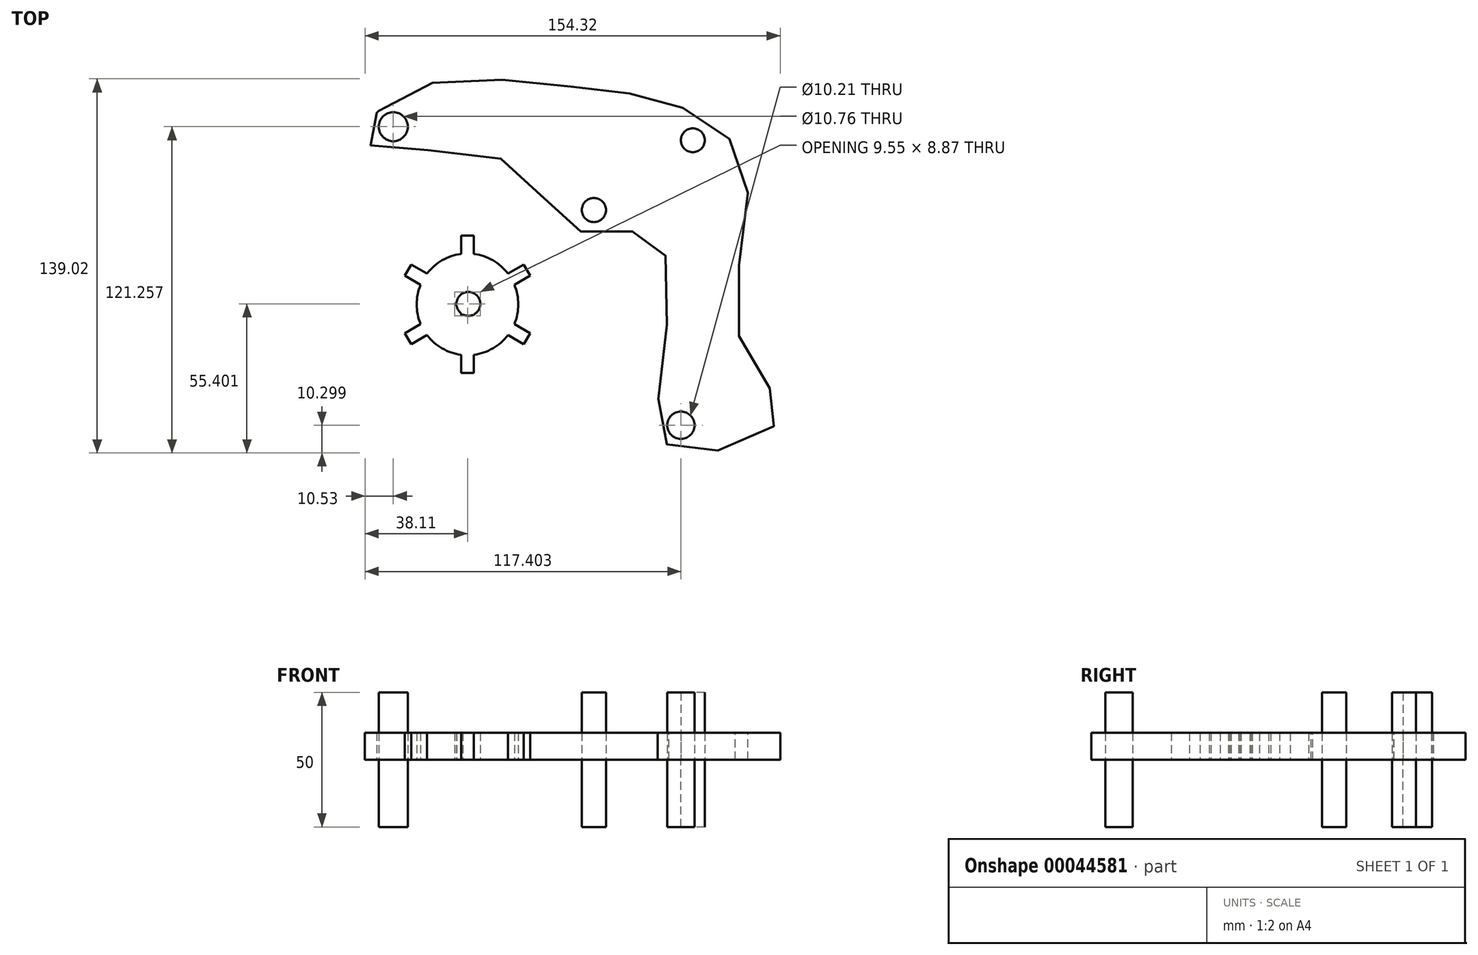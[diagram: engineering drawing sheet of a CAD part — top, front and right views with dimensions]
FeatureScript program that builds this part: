
annotation { "Feature Type Name" : "Feature", "Feature Type Description" : "" }
export const myFeature = defineFeature(function(context is Context, id is Id, definition is map)
    precondition{}
    {
        {
            var Q0;
            Q0=qCreatedBy(makeId("Top.planeOp"),FACE);
            var sketch = newSketch(context, id + "F0", { "sketchPlane" : qUnion([Q0])});
            skFitSpline(sketch, "E0", {"points": [v(-58.25, 62.71) * mm, v(0, 65.43) * mm, v(41.48, 58.63) * mm, v(69.05, 33.78) * mm, v(66.67, -28.5) * mm, v(81.3, -58.46) * mm, v(43.86, -70.37) * mm, v(37.05, -45.86) * mm, v(35.35, 8.93) * mm, v(6.08, 11.66) * mm, v(-21.15, 37.86) * mm, v(-71.52, 44) * mm, v(-58.25, 62.71) * mm]});
            skCircle(sketch, "E1", {"center": v(49.31, 45.07) * mm, "radius": 8 * mm});
            skCircle(sketch, "E2", {"center": v(44.88, -60.84) * mm, "radius": 8 * mm});
            skCircle(sketch, "E3", {"center": v(-62, 50.12) * mm, "radius": 8 * mm});
            skCircle(sketch, "E4", {"center": v(12.55, 19.14) * mm, "radius": 8 * mm});
            skLineSegment(sketch, "E5.rect.bottom", {"start": v(-32.04, -41.44) * mm, "end": v(-36.8, -41.44) * mm});
            skLineSegment(sketch, "E5.rect.top", {"start": v(-32.04, 9.61) * mm, "end": v(-36.8, 9.61) * mm});
            skLineSegment(sketch, "E5.rect.left", {"start": v(-32.04, -41.44) * mm, "end": v(-32.04, 9.61) * mm});
            skLineSegment(sketch, "E5.rect.right", {"start": v(-36.8, -41.44) * mm, "end": v(-36.8, 9.61) * mm});
            skPoint(sketch, "E5.rect.middle", {"position": v(-34.42, -15.91) * mm});
            skLineSegment(sketch, "E6.1.0", {"start": v(-55.34, -1.09) * mm, "end": v(-11.12, -26.61) * mm});
            skLineSegment(sketch, "E6.1.1", {"start": v(-57.72, -5.21) * mm, "end": v(-13.5, -30.74) * mm});
            skLineSegment(sketch, "E6.1.3", {"start": v(-13.5, -30.74) * mm, "end": v(-11.12, -26.61) * mm});
            skLineSegment(sketch, "E6.1.4", {"start": v(-57.72, -5.21) * mm, "end": v(-55.34, -1.09) * mm});
            skLineSegment(sketch, "E6.2.0", {"start": v(-11.12, -5.21) * mm, "end": v(-55.34, -30.74) * mm});
            skLineSegment(sketch, "E6.2.1", {"start": v(-13.5, -1.09) * mm, "end": v(-57.72, -26.61) * mm});
            skLineSegment(sketch, "E6.2.3", {"start": v(-57.72, -26.61) * mm, "end": v(-55.34, -30.74) * mm});
            skLineSegment(sketch, "E6.2.4", {"start": v(-13.5, -1.09) * mm, "end": v(-11.12, -5.21) * mm});
            skLineSegment(sketch, "E6.anchor1", {"start": v(-34.42, -15.91) * mm, "end": v(-36.8, -41.44) * mm, "construction": true});
            skLineSegment(sketch, "E6.anchor2", {"start": v(-34.42, -15.91) * mm, "end": v(-11.12, -5.21) * mm, "construction": true});
            skCircle(sketch, "E7", {"center": v(-34.42, -15.91) * mm, "radius": 18.88 * mm});
            skFitSpline(sketch, "E8.0", {"points": [v(-58.74, 59.44) * mm, v(-57.05, 60.37) * mm, v(-55.3, 61.2) * mm, v(-52.87, 62.2) * mm, v(-49.66, 63.22) * mm, v(-45.57, 64.13) * mm, v(-39.84, 64.96) * mm, v(-32.27, 65.36) * mm, v(-22.81, 65.05) * mm, v(-14.88, 64.37) * mm, v(-8.64, 63.71) * mm, v(-4.05, 63.2) * mm, v(0.42, 62.72) * mm, v(4.72, 62.28) * mm, v(8.85, 61.87) * mm, v(14.16, 61.33) * mm, v(20.48, 60.62) * mm, v(26.47, 59.7) * mm, v(31.13, 58.77) * mm, v(34.6, 57.95) * mm, v(38.03, 56.99) * mm, v(41.46, 55.86) * mm, v(44.9, 54.54) * mm, v(49.38, 52.54) * mm, v(54.68, 49.54) * mm, v(59.21, 45.83) * mm, v(62.18, 42.41) * mm, v(64.05, 39.62) * mm, v(65.27, 37.1) * mm, v(66.03, 34.92) * mm, v(66.48, 33.23) * mm, v(66.82, 31.44) * mm, v(67.12, 28.92) * mm, v(67.24, 25.54) * mm, v(67.04, 21.17) * mm, v(66.4, 15) * mm, v(65.09, 6.83) * mm, v(63.68, -1.66) * mm, v(62.84, -8.44) * mm, v(62.45, -13.5) * mm, v(62.39, -18.46) * mm, v(62.69, -22.5) * mm, v(63.2, -25.67) * mm, v(63.73, -28) * mm, v(64.43, -30.27) * mm, v(65.27, -32.44) * mm, v(66.24, -34.52) * mm, v(67.66, -37.18) * mm, v(69.6, -40.29) * mm, v(72.04, -43.7) * mm, v(74.37, -46.83) * mm, v(76.42, -49.69) * mm, v(78.02, -52.25) * mm, v(78.81, -54.07) * mm, v(79.1, -55.28) * mm, v(79.17, -56.06) * mm, v(79.11, -56.63) * mm, v(79, -57.07) * mm, v(78.87, -57.41) * mm, v(78.7, -57.77) * mm, v(78.4, -58.29) * mm, v(77.85, -59) * mm, v(76.95, -59.9) * mm, v(75.44, -61.12) * mm, v(73.03, -62.66) * mm, v(69.5, -64.35) * mm, v(65.55, -65.84) * mm, v(61.35, -67.04) * mm, v(57.1, -67.93) * mm, v(52.97, -68.44) * mm, v(49.8, -68.53) * mm, v(47.55, -68.4) * mm, v(46.02, -68.19) * mm, v(44.7, -67.88) * mm, v(43.6, -67.49) * mm, v(42.69, -67.02) * mm, v(41.93, -66.5) * mm, v(41.3, -65.89) * mm, v(40.56, -64.95) * mm, v(39.82, -63.49) * mm, v(39.22, -61.13) * mm, v(38.94, -58.18) * mm, v(38.95, -54.7) * mm, v(39.2, -50.76) * mm, v(39.65, -46.37) * mm, v(40.22, -41.6) * mm, v(41.05, -34.85) * mm, v(41.91, -27.74) * mm, v(42.58, -20.62) * mm, v(42.94, -15.37) * mm, v(43.1, -10.3) * mm, v(43, -5.48) * mm, v(42.58, -1) * mm, v(41.77, 3.1) * mm, v(40.67, 6.13) * mm, v(39.46, 8.3) * mm, v(38.54, 9.53) * mm, v(37.7, 10.41) * mm, v(37, 11.02) * mm, v(36.27, 11.57) * mm, v(35.24, 12.2) * mm, v(33.9, 12.81) * mm, v(31.66, 13.5) * mm, v(28.76, 13.87) * mm, v(25.2, 13.87) * mm, v(21.6, 13.63) * mm, v(18.01, 13.33) * mm, v(14.55, 13.12) * mm, v(11.87, 13.16) * mm, v(9.9, 13.37) * mm, v(8.54, 13.63) * mm, v(7.5, 13.94) * mm, v(6.73, 14.25) * mm, v(5.98, 14.6) * mm, v(5.06, 15.13) * mm, v(3.63, 16.17) * mm, v(1.87, 17.82) * mm, v(-0.22, 20.29) * mm, v(-2.33, 23.13) * mm, v(-4.53, 26.2) * mm, v(-6.91, 29.38) * mm, v(-9.56, 32.55) * mm, v(-12.08, 35.05) * mm, v(-14.34, 36.9) * mm, v(-16.16, 38.2) * mm, v(-17.8, 39.17) * mm, v(-19.18, 39.88) * mm, v(-20.62, 40.54) * mm, v(-22.5, 41.27) * mm, v(-24.84, 41.97) * mm, v(-27.27, 42.55) * mm, v(-30.6, 43.15) * mm, v(-34.88, 43.65) * mm, v(-40.14, 43.94) * mm, v(-45.39, 44.02) * mm, v(-50.5, 43.99) * mm, v(-55.34, 43.94) * mm, v(-59.77, 43.97) * mm, v(-63, 44.12) * mm, v(-65.21, 44.36) * mm, v(-66.66, 44.6) * mm, v(-67.86, 44.9) * mm, v(-68.62, 45.18) * mm, v(-69.07, 45.41) * mm, v(-69.32, 45.57) * mm, v(-69.5, 45.72) * mm, v(-69.61, 45.83) * mm, v(-69.7, 45.93) * mm, v(-69.77, 46.07) * mm, v(-69.85, 46.3) * mm, v(-69.9, 46.75) * mm, v(-69.82, 47.41) * mm, v(-69.59, 48.25) * mm, v(-69.04, 49.55) * mm, v(-67.92, 51.42) * mm, v(-65.92, 53.83) * mm, v(-63.38, 56.22) * mm, v(-60.9, 58.09) * mm, v(-58.74, 59.44) * mm, v(-57.05, 60.37) * mm, v(-55.3, 61.2) * mm]});
            skFitSpline(sketch, "E9.trimOffspring", {"points": [v(-58.74, 59.44) * mm, v(-57.05, 60.37) * mm, v(-55.3, 61.2) * mm, v(-52.87, 62.2) * mm, v(-49.66, 63.22) * mm, v(-45.57, 64.13) * mm, v(-39.84, 64.96) * mm, v(-32.27, 65.36) * mm, v(-22.81, 65.05) * mm, v(-14.88, 64.37) * mm, v(-8.64, 63.71) * mm, v(-4.05, 63.2) * mm, v(0.42, 62.72) * mm, v(4.72, 62.28) * mm, v(8.85, 61.87) * mm, v(14.16, 61.33) * mm, v(20.48, 60.62) * mm, v(26.47, 59.7) * mm, v(31.13, 58.77) * mm, v(34.6, 57.95) * mm, v(38.03, 56.99) * mm, v(41.46, 55.86) * mm, v(44.9, 54.54) * mm, v(49.38, 52.54) * mm, v(54.68, 49.54) * mm, v(59.21, 45.83) * mm, v(62.18, 42.41) * mm, v(64.05, 39.62) * mm, v(65.27, 37.1) * mm, v(66.03, 34.92) * mm, v(66.48, 33.23) * mm, v(66.82, 31.44) * mm, v(67.12, 28.92) * mm, v(67.24, 25.54) * mm, v(67.04, 21.17) * mm, v(66.4, 15) * mm, v(65.09, 6.83) * mm, v(63.68, -1.66) * mm, v(62.84, -8.44) * mm, v(62.45, -13.5) * mm, v(62.39, -18.46) * mm, v(62.69, -22.5) * mm, v(63.2, -25.67) * mm, v(63.73, -28) * mm, v(64.43, -30.27) * mm, v(65.27, -32.44) * mm, v(66.24, -34.52) * mm, v(67.66, -37.18) * mm, v(69.6, -40.29) * mm, v(72.04, -43.7) * mm, v(74.37, -46.83) * mm, v(76.42, -49.69) * mm, v(78.02, -52.25) * mm, v(78.81, -54.07) * mm, v(79.1, -55.28) * mm, v(79.17, -56.06) * mm, v(79.11, -56.63) * mm, v(79, -57.07) * mm, v(78.87, -57.41) * mm, v(78.7, -57.77) * mm, v(78.4, -58.29) * mm, v(77.85, -59) * mm, v(76.95, -59.9) * mm, v(75.44, -61.12) * mm, v(73.03, -62.66) * mm, v(69.5, -64.35) * mm, v(65.55, -65.84) * mm, v(61.35, -67.04) * mm, v(57.1, -67.93) * mm, v(52.97, -68.44) * mm, v(49.8, -68.53) * mm, v(47.55, -68.4) * mm, v(46.02, -68.19) * mm, v(44.7, -67.88) * mm, v(43.6, -67.49) * mm, v(42.69, -67.02) * mm, v(41.93, -66.5) * mm, v(41.3, -65.89) * mm, v(40.56, -64.95) * mm, v(39.82, -63.49) * mm, v(39.22, -61.13) * mm, v(38.94, -58.18) * mm, v(38.95, -54.7) * mm, v(39.2, -50.76) * mm, v(39.65, -46.37) * mm, v(40.22, -41.6) * mm, v(41.05, -34.85) * mm, v(41.91, -27.74) * mm, v(42.58, -20.62) * mm, v(42.94, -15.37) * mm, v(43.1, -10.3) * mm, v(43, -5.48) * mm, v(42.58, -1) * mm, v(41.77, 3.1) * mm, v(40.67, 6.13) * mm, v(39.46, 8.3) * mm, v(38.54, 9.53) * mm, v(37.7, 10.41) * mm, v(37, 11.02) * mm, v(36.27, 11.57) * mm, v(35.24, 12.2) * mm, v(33.9, 12.81) * mm, v(31.66, 13.5) * mm, v(28.76, 13.87) * mm, v(25.2, 13.87) * mm, v(21.6, 13.63) * mm, v(18.01, 13.33) * mm, v(14.55, 13.12) * mm, v(11.87, 13.16) * mm, v(9.9, 13.37) * mm, v(8.54, 13.63) * mm, v(7.5, 13.94) * mm, v(6.73, 14.25) * mm, v(5.98, 14.6) * mm, v(5.06, 15.13) * mm, v(3.63, 16.17) * mm, v(1.87, 17.82) * mm, v(-0.22, 20.29) * mm, v(-2.33, 23.13) * mm, v(-4.53, 26.2) * mm, v(-6.91, 29.38) * mm, v(-9.56, 32.55) * mm, v(-12.08, 35.05) * mm, v(-14.34, 36.9) * mm, v(-16.16, 38.2) * mm, v(-17.8, 39.17) * mm, v(-19.18, 39.88) * mm, v(-20.62, 40.54) * mm, v(-22.5, 41.27) * mm, v(-24.84, 41.97) * mm, v(-27.27, 42.55) * mm, v(-30.6, 43.15) * mm, v(-34.88, 43.65) * mm, v(-40.14, 43.94) * mm, v(-45.39, 44.02) * mm, v(-50.5, 43.99) * mm, v(-55.34, 43.94) * mm, v(-59.77, 43.97) * mm, v(-63, 44.12) * mm, v(-65.21, 44.36) * mm, v(-66.66, 44.6) * mm, v(-67.86, 44.9) * mm, v(-68.62, 45.18) * mm, v(-69.07, 45.41) * mm, v(-69.32, 45.57) * mm, v(-69.5, 45.72) * mm, v(-69.61, 45.83) * mm, v(-69.7, 45.93) * mm, v(-69.77, 46.07) * mm, v(-69.85, 46.3) * mm, v(-69.9, 46.75) * mm, v(-69.82, 47.41) * mm, v(-69.59, 48.25) * mm, v(-69.04, 49.55) * mm, v(-67.92, 51.42) * mm, v(-65.92, 53.83) * mm, v(-63.38, 56.22) * mm, v(-60.9, 58.09) * mm, v(-58.74, 59.44) * mm, v(-57.05, 60.37) * mm, v(-55.3, 61.2) * mm]});
            skFitSpline(sketch, "E10.trimOffspring", {"points": [v(-58.74, 59.44) * mm, v(-57.05, 60.37) * mm, v(-55.3, 61.2) * mm, v(-52.87, 62.2) * mm, v(-49.66, 63.22) * mm, v(-45.57, 64.13) * mm, v(-39.84, 64.96) * mm, v(-32.27, 65.36) * mm, v(-22.81, 65.05) * mm, v(-14.88, 64.37) * mm, v(-8.64, 63.71) * mm, v(-4.05, 63.2) * mm, v(0.42, 62.72) * mm, v(4.72, 62.28) * mm, v(8.85, 61.87) * mm, v(14.16, 61.33) * mm, v(20.48, 60.62) * mm, v(26.47, 59.7) * mm, v(31.13, 58.77) * mm, v(34.6, 57.95) * mm, v(38.03, 56.99) * mm, v(41.46, 55.86) * mm, v(44.9, 54.54) * mm, v(49.38, 52.54) * mm, v(54.68, 49.54) * mm, v(59.21, 45.83) * mm, v(62.18, 42.41) * mm, v(64.05, 39.62) * mm, v(65.27, 37.1) * mm, v(66.03, 34.92) * mm, v(66.48, 33.23) * mm, v(66.82, 31.44) * mm, v(67.12, 28.92) * mm, v(67.24, 25.54) * mm, v(67.04, 21.17) * mm, v(66.4, 15) * mm, v(65.09, 6.83) * mm, v(63.68, -1.66) * mm, v(62.84, -8.44) * mm, v(62.45, -13.5) * mm, v(62.39, -18.46) * mm, v(62.69, -22.5) * mm, v(63.2, -25.67) * mm, v(63.73, -28) * mm, v(64.43, -30.27) * mm, v(65.27, -32.44) * mm, v(66.24, -34.52) * mm, v(67.66, -37.18) * mm, v(69.6, -40.29) * mm, v(72.04, -43.7) * mm, v(74.37, -46.83) * mm, v(76.42, -49.69) * mm, v(78.02, -52.25) * mm, v(78.81, -54.07) * mm, v(79.1, -55.28) * mm, v(79.17, -56.06) * mm, v(79.11, -56.63) * mm, v(79, -57.07) * mm, v(78.87, -57.41) * mm, v(78.7, -57.77) * mm, v(78.4, -58.29) * mm, v(77.85, -59) * mm, v(76.95, -59.9) * mm, v(75.44, -61.12) * mm, v(73.03, -62.66) * mm, v(69.5, -64.35) * mm, v(65.55, -65.84) * mm, v(61.35, -67.04) * mm, v(57.1, -67.93) * mm, v(52.97, -68.44) * mm, v(49.8, -68.53) * mm, v(47.55, -68.4) * mm, v(46.02, -68.19) * mm, v(44.7, -67.88) * mm, v(43.6, -67.49) * mm, v(42.69, -67.02) * mm, v(41.93, -66.5) * mm, v(41.3, -65.89) * mm, v(40.56, -64.95) * mm, v(39.82, -63.49) * mm, v(39.22, -61.13) * mm, v(38.94, -58.18) * mm, v(38.95, -54.7) * mm, v(39.2, -50.76) * mm, v(39.65, -46.37) * mm, v(40.22, -41.6) * mm, v(41.05, -34.85) * mm, v(41.91, -27.74) * mm, v(42.58, -20.62) * mm, v(42.94, -15.37) * mm, v(43.1, -10.3) * mm, v(43, -5.48) * mm, v(42.58, -1) * mm, v(41.77, 3.1) * mm, v(40.67, 6.13) * mm, v(39.46, 8.3) * mm, v(38.54, 9.53) * mm, v(37.7, 10.41) * mm, v(37, 11.02) * mm, v(36.27, 11.57) * mm, v(35.24, 12.2) * mm, v(33.9, 12.81) * mm, v(31.66, 13.5) * mm, v(28.76, 13.87) * mm, v(25.2, 13.87) * mm, v(21.6, 13.63) * mm, v(18.01, 13.33) * mm, v(14.55, 13.12) * mm, v(11.87, 13.16) * mm, v(9.9, 13.37) * mm, v(8.54, 13.63) * mm, v(7.5, 13.94) * mm, v(6.73, 14.25) * mm, v(5.98, 14.6) * mm, v(5.06, 15.13) * mm, v(3.63, 16.17) * mm, v(1.87, 17.82) * mm, v(-0.22, 20.29) * mm, v(-2.33, 23.13) * mm, v(-4.53, 26.2) * mm, v(-6.91, 29.38) * mm, v(-9.56, 32.55) * mm, v(-12.08, 35.05) * mm, v(-14.34, 36.9) * mm, v(-16.16, 38.2) * mm, v(-17.8, 39.17) * mm, v(-19.18, 39.88) * mm, v(-20.62, 40.54) * mm, v(-22.5, 41.27) * mm, v(-24.84, 41.97) * mm, v(-27.27, 42.55) * mm, v(-30.6, 43.15) * mm, v(-34.88, 43.65) * mm, v(-40.14, 43.94) * mm, v(-45.39, 44.02) * mm, v(-50.5, 43.99) * mm, v(-55.34, 43.94) * mm, v(-59.77, 43.97) * mm, v(-63, 44.12) * mm, v(-65.21, 44.36) * mm, v(-66.66, 44.6) * mm, v(-67.86, 44.9) * mm, v(-68.62, 45.18) * mm, v(-69.07, 45.41) * mm, v(-69.32, 45.57) * mm, v(-69.5, 45.72) * mm, v(-69.61, 45.83) * mm, v(-69.7, 45.93) * mm, v(-69.77, 46.07) * mm, v(-69.85, 46.3) * mm, v(-69.9, 46.75) * mm, v(-69.82, 47.41) * mm, v(-69.59, 48.25) * mm, v(-69.04, 49.55) * mm, v(-67.92, 51.42) * mm, v(-65.92, 53.83) * mm, v(-63.38, 56.22) * mm, v(-60.9, 58.09) * mm, v(-58.74, 59.44) * mm, v(-57.05, 60.37) * mm, v(-55.3, 61.2) * mm]});
            skFitSpline(sketch, "E11.trimOffspring", {"points": [v(-58.74, 59.44) * mm, v(-57.05, 60.37) * mm, v(-55.3, 61.2) * mm, v(-52.87, 62.2) * mm, v(-49.66, 63.22) * mm, v(-45.57, 64.13) * mm, v(-39.84, 64.96) * mm, v(-32.27, 65.36) * mm, v(-22.81, 65.05) * mm, v(-14.88, 64.37) * mm, v(-8.64, 63.71) * mm, v(-4.05, 63.2) * mm, v(0.42, 62.72) * mm, v(4.72, 62.28) * mm, v(8.85, 61.87) * mm, v(14.16, 61.33) * mm, v(20.48, 60.62) * mm, v(26.47, 59.7) * mm, v(31.13, 58.77) * mm, v(34.6, 57.95) * mm, v(38.03, 56.99) * mm, v(41.46, 55.86) * mm, v(44.9, 54.54) * mm, v(49.38, 52.54) * mm, v(54.68, 49.54) * mm, v(59.21, 45.83) * mm, v(62.18, 42.41) * mm, v(64.05, 39.62) * mm, v(65.27, 37.1) * mm, v(66.03, 34.92) * mm, v(66.48, 33.23) * mm, v(66.82, 31.44) * mm, v(67.12, 28.92) * mm, v(67.24, 25.54) * mm, v(67.04, 21.17) * mm, v(66.4, 15) * mm, v(65.09, 6.83) * mm, v(63.68, -1.66) * mm, v(62.84, -8.44) * mm, v(62.45, -13.5) * mm, v(62.39, -18.46) * mm, v(62.69, -22.5) * mm, v(63.2, -25.67) * mm, v(63.73, -28) * mm, v(64.43, -30.27) * mm, v(65.27, -32.44) * mm, v(66.24, -34.52) * mm, v(67.66, -37.18) * mm, v(69.6, -40.29) * mm, v(72.04, -43.7) * mm, v(74.37, -46.83) * mm, v(76.42, -49.69) * mm, v(78.02, -52.25) * mm, v(78.81, -54.07) * mm, v(79.1, -55.28) * mm, v(79.17, -56.06) * mm, v(79.11, -56.63) * mm, v(79, -57.07) * mm, v(78.87, -57.41) * mm, v(78.7, -57.77) * mm, v(78.4, -58.29) * mm, v(77.85, -59) * mm, v(76.95, -59.9) * mm, v(75.44, -61.12) * mm, v(73.03, -62.66) * mm, v(69.5, -64.35) * mm, v(65.55, -65.84) * mm, v(61.35, -67.04) * mm, v(57.1, -67.93) * mm, v(52.97, -68.44) * mm, v(49.8, -68.53) * mm, v(47.55, -68.4) * mm, v(46.02, -68.19) * mm, v(44.7, -67.88) * mm, v(43.6, -67.49) * mm, v(42.69, -67.02) * mm, v(41.93, -66.5) * mm, v(41.3, -65.89) * mm, v(40.56, -64.95) * mm, v(39.82, -63.49) * mm, v(39.22, -61.13) * mm, v(38.94, -58.18) * mm, v(38.95, -54.7) * mm, v(39.2, -50.76) * mm, v(39.65, -46.37) * mm, v(40.22, -41.6) * mm, v(41.05, -34.85) * mm, v(41.91, -27.74) * mm, v(42.58, -20.62) * mm, v(42.94, -15.37) * mm, v(43.1, -10.3) * mm, v(43, -5.48) * mm, v(42.58, -1) * mm, v(41.77, 3.1) * mm, v(40.67, 6.13) * mm, v(39.46, 8.3) * mm, v(38.54, 9.53) * mm, v(37.7, 10.41) * mm, v(37, 11.02) * mm, v(36.27, 11.57) * mm, v(35.24, 12.2) * mm, v(33.9, 12.81) * mm, v(31.66, 13.5) * mm, v(28.76, 13.87) * mm, v(25.2, 13.87) * mm, v(21.6, 13.63) * mm, v(18.01, 13.33) * mm, v(14.55, 13.12) * mm, v(11.87, 13.16) * mm, v(9.9, 13.37) * mm, v(8.54, 13.63) * mm, v(7.5, 13.94) * mm, v(6.73, 14.25) * mm, v(5.98, 14.6) * mm, v(5.06, 15.13) * mm, v(3.63, 16.17) * mm, v(1.87, 17.82) * mm, v(-0.22, 20.29) * mm, v(-2.33, 23.13) * mm, v(-4.53, 26.2) * mm, v(-6.91, 29.38) * mm, v(-9.56, 32.55) * mm, v(-12.08, 35.05) * mm, v(-14.34, 36.9) * mm, v(-16.16, 38.2) * mm, v(-17.8, 39.17) * mm, v(-19.18, 39.88) * mm, v(-20.62, 40.54) * mm, v(-22.5, 41.27) * mm, v(-24.84, 41.97) * mm, v(-27.27, 42.55) * mm, v(-30.6, 43.15) * mm, v(-34.88, 43.65) * mm, v(-40.14, 43.94) * mm, v(-45.39, 44.02) * mm, v(-50.5, 43.99) * mm, v(-55.34, 43.94) * mm, v(-59.77, 43.97) * mm, v(-63, 44.12) * mm, v(-65.21, 44.36) * mm, v(-66.66, 44.6) * mm, v(-67.86, 44.9) * mm, v(-68.62, 45.18) * mm, v(-69.07, 45.41) * mm, v(-69.32, 45.57) * mm, v(-69.5, 45.72) * mm, v(-69.61, 45.83) * mm, v(-69.7, 45.93) * mm, v(-69.77, 46.07) * mm, v(-69.85, 46.3) * mm, v(-69.9, 46.75) * mm, v(-69.82, 47.41) * mm, v(-69.59, 48.25) * mm, v(-69.04, 49.55) * mm, v(-67.92, 51.42) * mm, v(-65.92, 53.83) * mm, v(-63.38, 56.22) * mm, v(-60.9, 58.09) * mm, v(-58.74, 59.44) * mm, v(-57.05, 60.37) * mm, v(-55.3, 61.2) * mm]});
            skCircle(sketch, "E12", {"center": v(-62, 50.12) * mm, "radius": 5.38 * mm});
            skCircle(sketch, "E13", {"center": v(12.55, 19.14) * mm, "radius": 4.5 * mm});
            skCircle(sketch, "E14", {"center": v(49.31, 45.07) * mm, "radius": 4.44 * mm});
            skCircle(sketch, "E15", {"center": v(44.88, -60.84) * mm, "radius": 5.1 * mm});
            skFitSpline(sketch, "E16.trimOffspring", {"points": [v(-58.74, 59.44) * mm, v(-57.05, 60.37) * mm, v(-55.3, 61.2) * mm, v(-52.87, 62.2) * mm, v(-49.66, 63.22) * mm, v(-45.57, 64.13) * mm, v(-39.84, 64.96) * mm, v(-32.27, 65.36) * mm, v(-22.81, 65.05) * mm, v(-14.88, 64.37) * mm, v(-8.64, 63.71) * mm, v(-4.05, 63.2) * mm, v(0.42, 62.72) * mm, v(4.72, 62.28) * mm, v(8.85, 61.87) * mm, v(14.16, 61.33) * mm, v(20.48, 60.62) * mm, v(26.47, 59.7) * mm, v(31.13, 58.77) * mm, v(34.6, 57.95) * mm, v(38.03, 56.99) * mm, v(41.46, 55.86) * mm, v(44.9, 54.54) * mm, v(49.38, 52.54) * mm, v(54.68, 49.54) * mm, v(59.21, 45.83) * mm, v(62.18, 42.41) * mm, v(64.05, 39.62) * mm, v(65.27, 37.1) * mm, v(66.03, 34.92) * mm, v(66.48, 33.23) * mm, v(66.82, 31.44) * mm, v(67.12, 28.92) * mm, v(67.24, 25.54) * mm, v(67.04, 21.17) * mm, v(66.4, 15) * mm, v(65.09, 6.83) * mm, v(63.68, -1.66) * mm, v(62.84, -8.44) * mm, v(62.45, -13.5) * mm, v(62.39, -18.46) * mm, v(62.69, -22.5) * mm, v(63.2, -25.67) * mm, v(63.73, -28) * mm, v(64.43, -30.27) * mm, v(65.27, -32.44) * mm, v(66.24, -34.52) * mm, v(67.66, -37.18) * mm, v(69.6, -40.29) * mm, v(72.04, -43.7) * mm, v(74.37, -46.83) * mm, v(76.42, -49.69) * mm, v(78.02, -52.25) * mm, v(78.81, -54.07) * mm, v(79.1, -55.28) * mm, v(79.17, -56.06) * mm, v(79.11, -56.63) * mm, v(79, -57.07) * mm, v(78.87, -57.41) * mm, v(78.7, -57.77) * mm, v(78.4, -58.29) * mm, v(77.85, -59) * mm, v(76.95, -59.9) * mm, v(75.44, -61.12) * mm, v(73.03, -62.66) * mm, v(69.5, -64.35) * mm, v(65.55, -65.84) * mm, v(61.35, -67.04) * mm, v(57.1, -67.93) * mm, v(52.97, -68.44) * mm, v(49.8, -68.53) * mm, v(47.55, -68.4) * mm, v(46.02, -68.19) * mm, v(44.7, -67.88) * mm, v(43.6, -67.49) * mm, v(42.69, -67.02) * mm, v(41.93, -66.5) * mm, v(41.3, -65.89) * mm, v(40.56, -64.95) * mm, v(39.82, -63.49) * mm, v(39.22, -61.13) * mm, v(38.94, -58.18) * mm, v(38.95, -54.7) * mm, v(39.2, -50.76) * mm, v(39.65, -46.37) * mm, v(40.22, -41.6) * mm, v(41.05, -34.85) * mm, v(41.91, -27.74) * mm, v(42.58, -20.62) * mm, v(42.94, -15.37) * mm, v(43.1, -10.3) * mm, v(43, -5.48) * mm, v(42.58, -1) * mm, v(41.77, 3.1) * mm, v(40.67, 6.13) * mm, v(39.46, 8.3) * mm, v(38.54, 9.53) * mm, v(37.7, 10.41) * mm, v(37, 11.02) * mm, v(36.27, 11.57) * mm, v(35.24, 12.2) * mm, v(33.9, 12.81) * mm, v(31.66, 13.5) * mm, v(28.76, 13.87) * mm, v(25.2, 13.87) * mm, v(21.6, 13.63) * mm, v(18.01, 13.33) * mm, v(14.55, 13.12) * mm, v(11.87, 13.16) * mm, v(9.9, 13.37) * mm, v(8.54, 13.63) * mm, v(7.5, 13.94) * mm, v(6.73, 14.25) * mm, v(5.98, 14.6) * mm, v(5.06, 15.13) * mm, v(3.63, 16.17) * mm, v(1.87, 17.82) * mm, v(-0.22, 20.29) * mm, v(-2.33, 23.13) * mm, v(-4.53, 26.2) * mm, v(-6.91, 29.38) * mm, v(-9.56, 32.55) * mm, v(-12.08, 35.05) * mm, v(-14.34, 36.9) * mm, v(-16.16, 38.2) * mm, v(-17.8, 39.17) * mm, v(-19.18, 39.88) * mm, v(-20.62, 40.54) * mm, v(-22.5, 41.27) * mm, v(-24.84, 41.97) * mm, v(-27.27, 42.55) * mm, v(-30.6, 43.15) * mm, v(-34.88, 43.65) * mm, v(-40.14, 43.94) * mm, v(-45.39, 44.02) * mm, v(-50.5, 43.99) * mm, v(-55.34, 43.94) * mm, v(-59.77, 43.97) * mm, v(-63, 44.12) * mm, v(-65.21, 44.36) * mm, v(-66.66, 44.6) * mm, v(-67.86, 44.9) * mm, v(-68.62, 45.18) * mm, v(-69.07, 45.41) * mm, v(-69.32, 45.57) * mm, v(-69.5, 45.72) * mm, v(-69.61, 45.83) * mm, v(-69.7, 45.93) * mm, v(-69.77, 46.07) * mm, v(-69.85, 46.3) * mm, v(-69.9, 46.75) * mm, v(-69.82, 47.41) * mm, v(-69.59, 48.25) * mm, v(-69.04, 49.55) * mm, v(-67.92, 51.42) * mm, v(-65.92, 53.83) * mm, v(-63.38, 56.22) * mm, v(-60.9, 58.09) * mm, v(-58.74, 59.44) * mm, v(-57.05, 60.37) * mm, v(-55.3, 61.2) * mm]});
            skCircle(sketch, "E17", {"center": v(-34.07, -15.74) * mm, "radius": 4.44 * mm});
            skPoint(sketch, "E18", {"position": v(-36.45, -12) * mm});
            skPoint(sketch, "E19", {"position": v(-45.83, -0.87) * mm});
            skSolve(sketch);
        }
        {
            var Q0;
            Q0 = qSketchRegion(id + "F0", true);
            var Q1;
            Q1=makeQuery(id+"F0.imprint","IMPRINT",FACE,{"disambiguationData":[TD([[makeQuery(id+"F0.imprint","IMPRINT",EDGE,{"derivedFrom":sQuery(id+"F0.wireOp",EDGE,"E13")}),-1.0]])]});
            var Q2;
            Q2=makeQuery(id+"F0.imprint","IMPRINT",FACE,{"disambiguationData":[TD([[makeQuery(id+"F0.imprint","IMPRINT",EDGE,{"derivedFrom":sQuery(id+"F0.wireOp",EDGE,"E1")}),1.0]])]});
            var Q3;
            Q3=makeQuery(id+"F0.imprint","IMPRINT",FACE,{"disambiguationData":[TD([[makeQuery(id+"F0.imprint","IMPRINT",EDGE,{"derivedFrom":sQuery(id+"F0.wireOp",EDGE,"E15")}),-1.0]])]});
            extrude(context, id + "F1", {"entities" : qUnion([Q0, Q1, Q2, Q3]), "depth" : 10 * mm});
        }
        {
            var Q0;
            Q0=makeQuery(id+"F0.imprint","IMPRINT",FACE,{"disambiguationData":[TD([[makeQuery(id+"F0.imprint","IMPRINT",EDGE,{"derivedFrom":sQuery(id+"F0.wireOp",EDGE,"E13")}),1.0]])]});
            var Q1;
            Q1=makeQuery(id+"F0.imprint","IMPRINT",FACE,{"disambiguationData":[TD([[makeQuery(id+"F0.imprint","IMPRINT",EDGE,{"derivedFrom":sQuery(id+"F0.wireOp",EDGE,"E12")}),1.0]])]});
            var Q2;
            Q2=makeQuery(id+"F0.imprint","IMPRINT",FACE,{"disambiguationData":[TD([[makeQuery(id+"F0.imprint","IMPRINT",EDGE,{"derivedFrom":sQuery(id+"F0.wireOp",EDGE,"E15")}),1.0]])]});
            var Q3;
            Q3=makeQuery(id+"F0.imprint","IMPRINT",FACE,{"disambiguationData":[TD([[makeQuery(id+"F0.imprint","IMPRINT",EDGE,{"derivedFrom":sQuery(id+"F0.wireOp",EDGE,"E14")}),1.0]])]});
            extrude(context, id + "F2", {"entities" : qUnion([Q0, Q1, Q2, Q3]), "operationType" : NewBodyOperationType.ADD, "oppositeDirection" : true, "depth" : 25 * mm});
        }
        {
            var Q0;
            Q0=makeQuery(id+"F2.opExtrude","SWEPT_BODY",BODY,{"disambiguationData":[OSD([sQuery(id+"F0.wireOp",EDGE,"E12")])]});
            var Q1;
            Q1=makeQuery(id+"F2.opExtrude","SWEPT_BODY",BODY,{"disambiguationData":[OSD([sQuery(id+"F0.wireOp",EDGE,"E14")])]});
            var Q2;
            Q2=makeQuery(id+"F2.opExtrude","SWEPT_BODY",BODY,{"disambiguationData":[OSD([sQuery(id+"F0.wireOp",EDGE,"E15")])]});
            var Q3;
            Q3=makeQuery(id+"F2.opExtrude","SWEPT_BODY",BODY,{"disambiguationData":[OSD([sQuery(id+"F0.wireOp",EDGE,"E13")])]});
            var Q4;
            Q4=qCreatedBy(makeId("Top.planeOp"),FACE);
            mirror(context, id + "F3", {"entities" : qUnion([Q0, Q1, Q2, Q3]), "mirrorPlane" : qUnion([Q4])});
        }
    });
